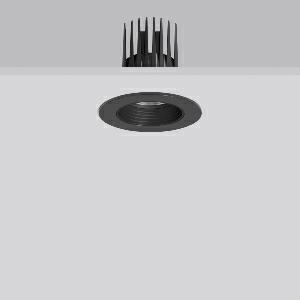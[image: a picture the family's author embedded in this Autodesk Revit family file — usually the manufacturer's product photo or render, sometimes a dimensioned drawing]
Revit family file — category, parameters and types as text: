
# Revit family: heledon_mini_e_901743_003_1_76_5beb
name_source: partatom
category: Lighting Fixtures
units: mm (PartAtom-declared; Revit-internal decimal feet)

## family parameters
Cut with Voids When Loaded = No
Host = Face
Light Source = No
Part Type = Normal
Room Calculation Point = No
Round Connector Dimension = Use Diameter
Shared = No

## types (1)
- HELEDON mini E (1 x LED Modul 940, 2400 lm, 4000)
    Apparent Load = 20 VA
    Approval mark = CE
    CIE Flux Codes = 99 100 100 100 100
    Color Rendering = 92
    Color Temperature = 4000
    Default Elevation = 1800 mm
    Description = Series: HELEDON mini
Round recessed downlight. Housing: die-cast aluminium, powder-coated. Black plastic ring and recessed LED to prevent glare from the side. Optical assembly with lens made of plastic (polycarbonate) for the best homogeneous light distribution - can be changed without tools. Best colour rendering index Ra>90. Suitable for Recessed ceiling mounting. Installation without tools thanks to spring fastening system. Including separate LED converter with connecting cable 600 mm.High quality converter without flickering and stroboscopic effect. Through-wiring box (5 pole) available as accessory. The following accessories can be mounted without use of tools: interchangeable lenses, decorative glasses, honeycomb louvre, clear and frosted diffusers, white interchangeable plastic ring. 
Colour: deep black, matt (RAL 9005)
Diameter: 124 mm
Height: 3 mm
Cut-out diameter: 114 mm
Recess height: 170 mm
Luminaire: recess height: 120 mm
Lamp: LED
Socket: without socket
Colour temperature: 4000K
Colour rendering index (CRI): 92
System power: 20 W
Rated luminous flux: 2400 lm
Luminous efficiency: 120 lm/W
Control gear: Converter, dimmable, DALI
Protection class: II
Type of protection: IP 20
    Height = 0 mm  [stored 0 ft]
    Lamp = 1 x LED Modul 940
    Lamp Light Flux = 2400 lm
    Lamp count = 1
    Length = 124 mm  [stored 0.406824 ft]
    Lifetime = 50000 h
    Luminous efficacy = 120 lm/W
    Manufacturer = RZB
    ModVariant = No
    Model = 901743.003.1.76
    Mounting Place = Ceiling
    Mounting Type = Recessed
    Number of Poles = 1
    OnlyDefault = Yes
    Power Factor = 1
    Product Name = HELEDON mini E
    Product group = Recessed downlights
    ProductGroupID = 402
    Protection Class = Protection class II
    Protection Degree = IP 20
    RLX_Detail_Level = 1
    RLX_Emergency_Light_Flux = 0 lm
    RLX_Emergency_Type = 0
    RLX_Emergency_Type_DB = No
    RlxData = <blob elided: 126317 chars, md5=307b58ab>
    Socket = socket
    Standby Power = 0 W
    System Light Flux = 2400 lm
    System Power = 20 W
    Type Comments = Product without accessories
    Type Image = 901656.003.jpg
    URL = http://relux.com
    VarID = ---
    Voltage = 230 V
    Voltage Range = 220-240 V
    Weight = 0.00 kg
    Width = 0 mm  [stored 0 ft]

note: [stored X ft] marks values corroborated as IEEE doubles in the binary element streams (Revit-internal decimal feet)

## geometry (parser evidence)
native form markers: Blend x4, Sweep x12
no freeform markers — native parametric forms only
